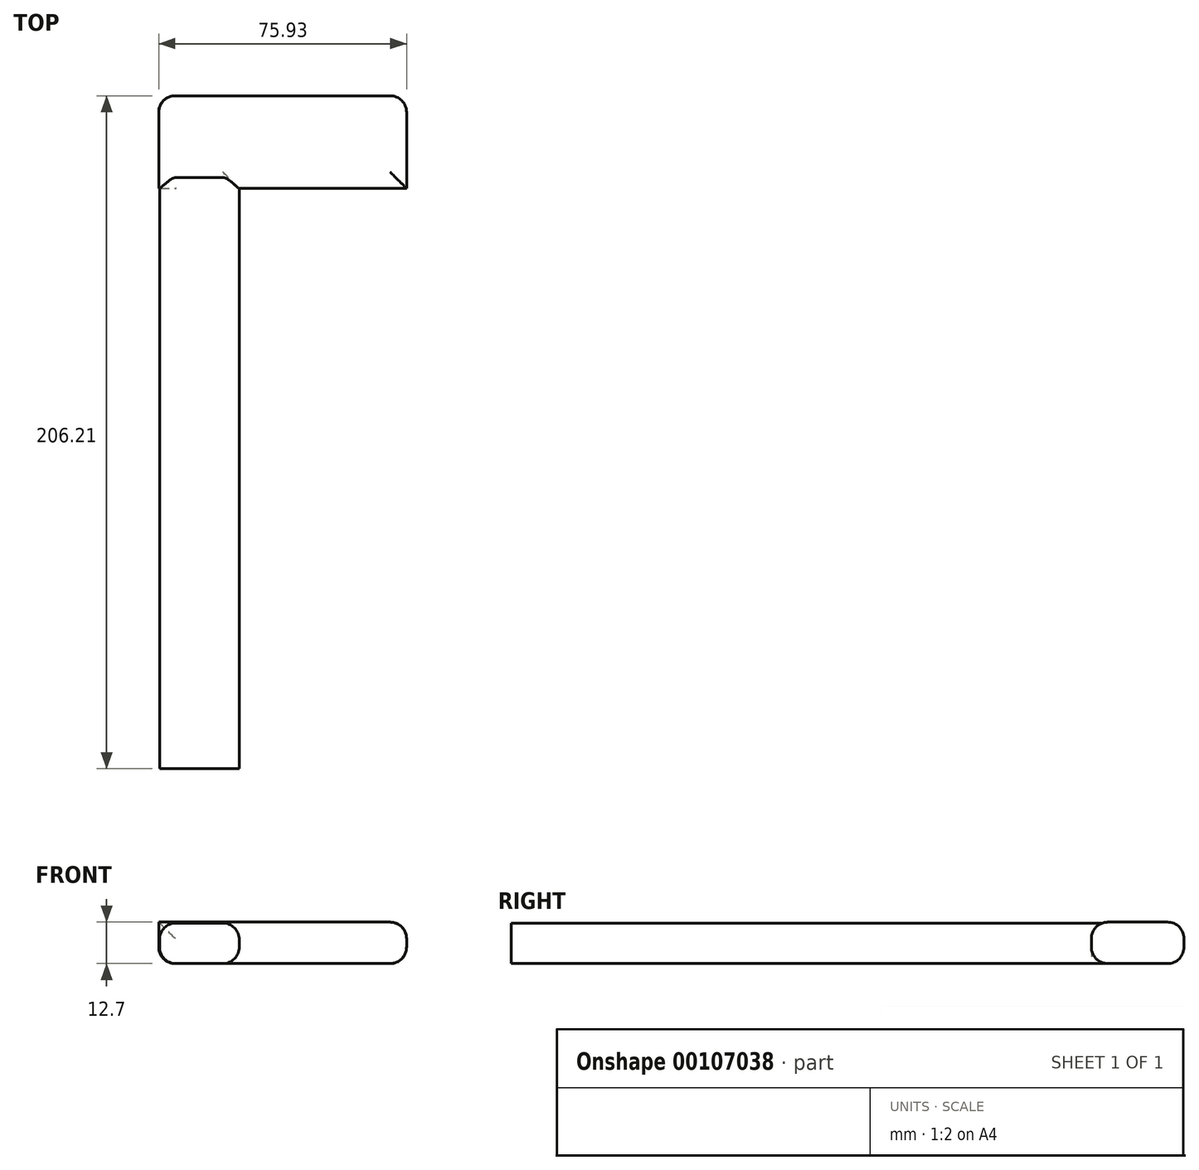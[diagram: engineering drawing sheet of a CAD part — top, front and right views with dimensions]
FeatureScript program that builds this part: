
annotation { "Feature Type Name" : "Feature", "Feature Type Description" : "" }
export const myFeature = defineFeature(function(context is Context, id is Id, definition is map)
    precondition{}
    {
        {
            var Q0;
            Q0=qCreatedBy(makeId("Top.planeOp"),FACE);
            var sketch = newSketch(context, id + "F0", { "sketchPlane" : qUnion([Q0])});
            skLineSegment(sketch, "E0.bottom", {"start": v(0, 0) * mm, "end": v(-75.93, 0) * mm});
            skLineSegment(sketch, "E0.top", {"start": v(0, 28.41) * mm, "end": v(-75.93, 28.41) * mm});
            skLineSegment(sketch, "E0.left", {"start": v(0, 0) * mm, "end": v(0, 28.41) * mm});
            skLineSegment(sketch, "E0.right", {"start": v(-75.93, 0) * mm, "end": v(-75.93, 28.41) * mm});
            skSolve(sketch);
        }
        {
            var Q0;
            Q0=makeQuery(id+"F0.imprint","IMPRINT",FACE,{"disambiguationData":[TD([[makeQuery(id+"F0.imprint","IMPRINT",EDGE,{"derivedFrom":sQuery(id+"F0.wireOp",EDGE,"E0.bottom")}),-1.0]])]});
            extrude(context, id + "F1", {"entities" : qUnion([Q0]), "depth" : 12.7 * mm});
        }
        {
            var Q0;
            Q0=qCreatedBy(makeId("Front.planeOp"),FACE);
            var sketch = newSketch(context, id + "F2", { "sketchPlane" : qUnion([Q0])});
            skLineSegment(sketch, "E1.bottom", {"start": v(-75.7, 0) * mm, "end": v(-51.28, 0) * mm});
            skLineSegment(sketch, "E1.top", {"start": v(-75.7, 12.41) * mm, "end": v(-51.28, 12.41) * mm});
            skLineSegment(sketch, "E1.left", {"start": v(-75.7, 0) * mm, "end": v(-75.7, 12.41) * mm});
            skLineSegment(sketch, "E1.right", {"start": v(-51.28, 0) * mm, "end": v(-51.28, 12.41) * mm});
            skSolve(sketch);
        }
        {
            var Q0;
            Q0=makeQuery(id+"F2.imprint","IMPRINT",FACE,{"disambiguationData":[TD([[makeQuery(id+"F2.imprint","IMPRINT",EDGE,{"derivedFrom":sQuery(id+"F2.wireOp",EDGE,"E1.bottom")}),1.0]])]});
            extrude(context, id + "F3", {"entities" : qUnion([Q0]), "operationType" : NewBodyOperationType.ADD, "depth" : 177.8 * mm});
        }
        {
            var Q0;
            Q0=makeQuery(id+"F1.opExtrude","CAP_EDGE",EDGE,{"disambiguationData":[OSD([sQuery(id+"F0.wireOp",EDGE,"E0.left")])],"isStart":true});
            var Q1;
            {var subQ0=sQuery(id+"F0.wireOp",EDGE,"E0.left");var subQ1=sQuery(id+"F0.wireOp",EDGE,"E0.bottom");Q1=makeQuery(id+"F3.boolean.opBoolean","SPLIT",EDGE,{"disambiguationData":[TD([makeQuery(id+"F1.opExtrude","SWEPT_FACE",FACE,{"disambiguationData":[OSD([subQ0])]})])],"derivedFrom":makeQuery(id+"F1.opExtrude","CAP_EDGE",EDGE,{"disambiguationData":[OSD([subQ1])],"isStart":true})});}
            var Q2;
            Q2=makeQuery(id+"F1.opExtrude","CAP_EDGE",EDGE,{"disambiguationData":[OSD([sQuery(id+"F0.wireOp",EDGE,"E0.bottom")])],"isStart":false});
            var Q3;
            Q3=makeQuery(id+"F1.opExtrude","CAP_EDGE",EDGE,{"disambiguationData":[OSD([sQuery(id+"F0.wireOp",EDGE,"E0.left")])],"isStart":false});
            var Q4;
            Q4=makeQuery(id+"F3.opExtrude","SWEPT_EDGE",EDGE,{"disambiguationData":[OSD([sQuery(id+"F2.wireOp",EDGE,"E1.bottom"),sQuery(id+"F2.wireOp",EDGE,"E1.right")])]});
            fillet(context, id + "F4", {"entities" : qUnion([Q0, Q1, Q2, Q3, Q4]), "radius" : 5.08 * mm, "tangentPropagation" : true, "allowEdgeOverflow" : false});
        }
        {
            var Q0;
            Q0=makeQuery(id+"F3.opExtrude","SWEPT_EDGE",EDGE,{"disambiguationData":[OSD([sQuery(id+"F2.wireOp",EDGE,"E1.top"),sQuery(id+"F2.wireOp",EDGE,"E1.right")])]});
            var Q1;
            Q1=makeQuery(id+"F3.opExtrude","SWEPT_EDGE",EDGE,{"disambiguationData":[OSD([sQuery(id+"F2.wireOp",EDGE,"E1.top"),sQuery(id+"F2.wireOp",EDGE,"E1.left")])]});
            var Q2;
            Q2=makeQuery(id+"F3.opExtrude","SWEPT_EDGE",EDGE,{"disambiguationData":[OSD([sQuery(id+"F2.wireOp",EDGE,"E1.bottom"),sQuery(id+"F2.wireOp",EDGE,"E1.left")])]});
            fillet(context, id + "F5", {"entities" : qUnion([Q0, Q1, Q2]), "radius" : 5.08 * mm, "tangentPropagation" : true, "allowEdgeOverflow" : false});
        }
        {
            var Q0;
            Q0=makeQuery(id+"F1.opExtrude","CAP_EDGE",EDGE,{"disambiguationData":[OSD([sQuery(id+"F0.wireOp",EDGE,"E0.right")])],"isStart":true});
            var Q1;
            Q1=makeQuery(id+"F1.opExtrude","SWEPT_EDGE",EDGE,{"disambiguationData":[OSD([sQuery(id+"F0.wireOp",EDGE,"E0.top"),sQuery(id+"F0.wireOp",EDGE,"E0.right")])]});
            var Q2;
            Q2=makeQuery(id+"F1.opExtrude","CAP_EDGE",EDGE,{"disambiguationData":[OSD([sQuery(id+"F0.wireOp",EDGE,"E0.top")])],"isStart":true});
            fillet(context, id + "F6", {"entities" : qUnion([Q0, Q1, Q2]), "radius" : 5.08 * mm, "tangentPropagation" : true, "allowEdgeOverflow" : false});
        }
    });
